# Revit family: ledroadlight-e_80w-4000_705000021800
name_source: partatom
category: Leuchten
revit_build: Autodesk Revit 2016 (Build: 20190508_0715(x64)
units: mm (PartAtom-declared; Revit-internal decimal feet)

## family parameters
Basisbauteil = Fläche
Beim Laden mit Abzugskörper schneiden = Nein
Bemaßung runder Anschluss = Durchmesser verwenden
Gemeinsam genutzt = Nein
Lichtquelle = Nein
Raumberechnungspunkt = Nein
Teiletyp = Normal

## types (1)
- LEDRoadlight-E 80W-4000 (1 x LED, 10000 lm)
    Approval mark = CE, ENEC
    Beschreibung = Sleek and compact Roadlight solution. Up to 60% energy saving compared to traditional roadlights. Advanced optical design optimized for road lighting. Accessories available for many pole types and connections. Robust die-cast aluminium body. IP66 and suitable for use on the coastal applications.
    CIE Flux Codes = 42 76 98 100 100
    Control Gear = Electronic ballast
    Height = 870 mm
    Hersteller = OPPLE
    Lamp Light Flux = 10000 lm
    Lamp count = 1
    Lampe = 1 x LED
    Length = 5050 mm
    Luminous efficacy = 125 lm/W
    ModVariant = Nein
    Modell = 705000021800
    Mounting Place = Pole
    Mounting Type = Pole top, Pole annexe
    Number of Poles = 1
    OnlyDefault = Ja
    Power Factor = 1
    Product Name = LEDRoadlight-E 80W-4000
    Product group = Roadlight EcoMax
    ProductGroupID = 6230
    Protection Class = Protection class I
    Protection Degree = IP 66
    RLX_Detail_Level = 1
    RlxData = <blob elided: 242501 chars, md5=81f3b2e9>
    Scheinlast = 80 VA
    Socket = socket
    Standby Power = 0 W
    System Light Flux = 10000 lm
    System Power = 80 W
    Typenbild = 705000021800.jpg
    Typenkommentare = Product without accessories
    URL = http://relux.com
    VarID = ---
    Voltage = 0 V
    Vorgabe-Ansicht = 1800 mm
    Weight = 0.00 kg
    Width = 2350 mm

## geometry (parser evidence)
native form markers: Sweep x10
no freeform markers — native parametric forms only
